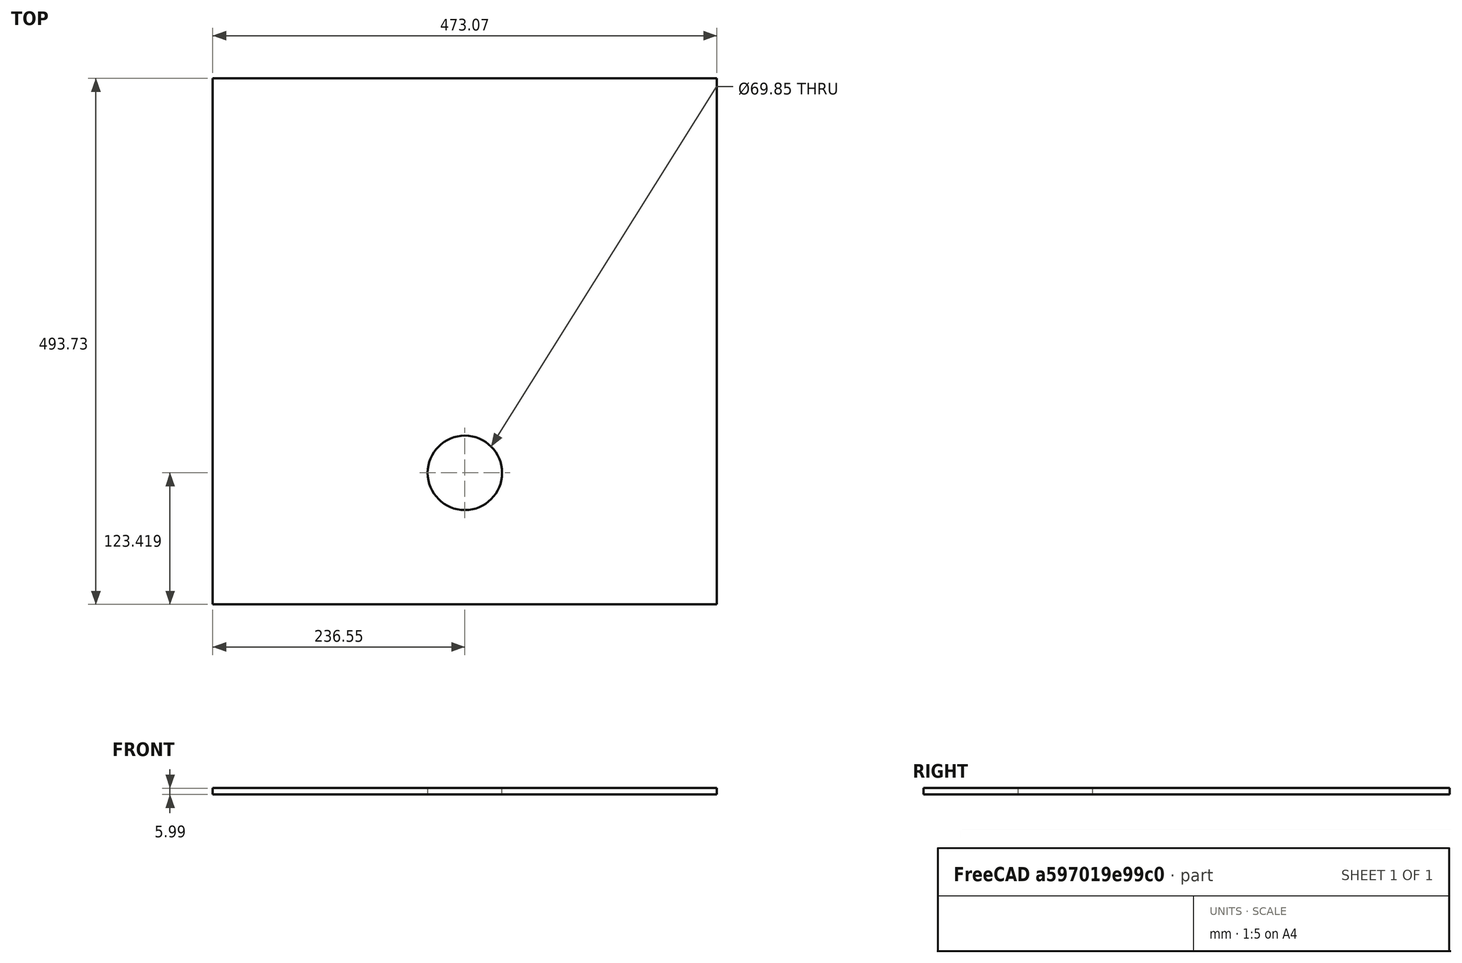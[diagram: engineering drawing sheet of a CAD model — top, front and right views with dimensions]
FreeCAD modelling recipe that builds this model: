
FCSTD DOCUMENT  (FreeCAD 0.19R24267 (Git))
Label: Up1-P3
License: All rights reserved
LicenseURL: http://en.wikipedia.org/wiki/All_rights_reserved
objects: TechDraw::DrawViewDimension×6, TechDraw::DrawProjGroupItem×2, TechDraw::DrawViewAnnotation×2, TechDraw::DrawHatch×2, Sketcher::SketchObject×1, Part::Extrusion×1, TechDraw::DrawSVGTemplate×1, TechDraw::DrawProjGroup×1, TechDraw::DrawPage×1
note: 2 computed .brp shape members not serialized (recipe doc carries the construction recipe); baked Part::Feature solids carry a one-line shape summary decoded from their .brp

FEATURE [Sketcher::SketchObject] Sketch
  FullyConstrained = true
  Placement = pos=(0,0,762) rot=(0,0,1;0rad)
  sketch-geometry (5):
    g0: LineSegment StartX=0 StartY=0 StartZ=0 EndX=473.075 EndY=0 EndZ=0
    g1: LineSegment StartX=473.075 StartY=0 StartZ=0 EndX=473.075 EndY=493.725 EndZ=0
    g2: LineSegment StartX=473.075 StartY=493.725 StartZ=0 EndX=0 EndY=493.725 EndZ=0
    g3: LineSegment StartX=0 StartY=493.725 StartZ=0 EndX=0 EndY=0 EndZ=0
    g4: Circle CenterX=236.55 CenterY=123.419 CenterZ=0 NormalX=0 NormalY=0 NormalZ=1 AngleXU=0 Radius=34.925
  constraints (14):
    c: Coincident(g0,g1)
    c: Coincident(g1,g2)
    c: Coincident(g2,g3)
    c: Coincident(g3,g0)
    c: Horizontal(g0)
    c: Horizontal(g2)
    c: Vertical(g1)
    c: Vertical(g3)
    c: Coincident(g0,g-1)
    c: DistanceX(g2,g2) = 473.075
    c: DistanceY(g3,g3) = 493.725
    c: DistanceY(g0,g4) = 123.419
    c: Distance(g4,g3) = 236.55
    c: Diameter(g4) = 69.85
FEATURE [Part::Extrusion] Extrude
  Base = -> Sketch
  Dir = (0,0,1)
  DirMode = 2
  FaceMakerClass = Part::FaceMakerBullseye
  LengthFwd = 5.9944
  LengthRev = 0
  Solid = true
  Symmetric = false
FEATURE [TechDraw::DrawSVGTemplate] Template
  Height = 215.9
  Orientation = 1
  Width = 279.4
FEATURE [TechDraw::DrawProjGroupItem] ProjItem  label="Front"
  CoarseView = false
  Direction = (0,0,1)
  Focus = 100
  HardHidden = false
  IsoCount = 0
  IsoHidden = false
  IsoVisible = false
  LockPosition = true
  Perspective = false
  Rotation = 0
  RotationVector = (1,0,0)
  Scale = 0.25
  ScaleType = 2
  SeamHidden = false
  SeamVisible = true
  SmoothHidden = false
  SmoothVisible = true
  Source = -> [Extrude]
  Type = 0
  X = 0
  XDirection = (1,0,0)
  Y = 0
FEATURE [TechDraw::DrawProjGroupItem] ProjItem001  label="Left"
  CoarseView = false
  Direction = (-1,0,1e-16)
  Focus = 100
  HardHidden = false
  IsoCount = 0
  IsoHidden = false
  IsoVisible = false
  LockPosition = false
  Perspective = false
  Rotation = 0
  RotationVector = (1,0,0)
  ScaleType = 2
  SeamHidden = false
  SeamVisible = true
  SmoothHidden = false
  SmoothVisible = true
  Source = -> [Extrude]
  Type = 1
  X = 88.5859
  XDirection = (1e-16,0,1)
  Y = 0
FEATURE [TechDraw::DrawProjGroup] ProjGroup
  Anchor = -> ProjItem
  AutoDistribute = true
  LockPosition = false
  ProjectionType = 0
  Rotation = 0
  Scale = 0.25
  ScaleType = 2
  Source = -> [Extrude]
  Views = -> [ProjItem,ProjItem001]
  X = 139.7
  Y = 107.95
  spacingX = 15.0114
  spacingY = 15.0114
FEATURE [TechDraw::DrawViewDimension] Dimension
  Arbitrary = false
  ArbitraryTolerances = false
  EqualTolerance = true
  FormatSpec = %.3f
  FormatSpecOverTolerance = %+.3f
  FormatSpecUnderTolerance = %+.3f
  Inverted = false
  LockPosition = false
  MeasureType = 1
  OverTolerance = 0
  References2D = -> [ProjItem]
  Rotation = 0
  ScaleType = 0
  TheoreticalExact = false
  Type = 1
  UnderTolerance = 0
  X = 0.805815
  Y = -69.7738
FEATURE [TechDraw::DrawViewDimension] Dimension001
  Arbitrary = false
  ArbitraryTolerances = false
  EqualTolerance = true
  FormatSpec = %.3f
  FormatSpecOverTolerance = %+.3f
  FormatSpecUnderTolerance = %+.3f
  Inverted = false
  LockPosition = false
  MeasureType = 1
  OverTolerance = 0
  References2D = -> [ProjItem001]
  Rotation = 0
  ScaleType = 0
  TheoreticalExact = false
  Type = 1
  UnderTolerance = 0
  X = 13.7182
  Y = 46.5357
FEATURE [TechDraw::DrawViewDimension] Dimension002
  Arbitrary = false
  ArbitraryTolerances = false
  EqualTolerance = true
  FormatSpec = %.3f
  FormatSpecOverTolerance = %+.3f
  FormatSpecUnderTolerance = %+.3f
  Inverted = false
  LockPosition = false
  MeasureType = 1
  OverTolerance = 0
  References2D = -> [ProjItem]
  Rotation = 0
  ScaleType = 0
  TheoreticalExact = false
  Type = 2
  UnderTolerance = 0
  X = 66.3867
  Y = 0.402907
FEATURE [TechDraw::DrawViewDimension] Dimension003
  Arbitrary = false
  ArbitraryTolerances = false
  EqualTolerance = true
  FormatSpec = %.3f
  FormatSpecOverTolerance = %+.3f
  FormatSpecUnderTolerance = %+.3f
  Inverted = false
  LockPosition = false
  MeasureType = 1
  OverTolerance = 0
  References2D = -> [ProjItem]
  Rotation = 0
  ScaleType = 0
  TheoreticalExact = false
  Type = 2
  UnderTolerance = 0
  X = 17.3858
  Y = -44.692
FEATURE [TechDraw::DrawViewDimension] Dimension004
  Arbitrary = false
  ArbitraryTolerances = false
  EqualTolerance = true
  FormatSpec = %.3f
  FormatSpecOverTolerance = %+.3f
  FormatSpecUnderTolerance = %+.3f
  Inverted = false
  LockPosition = false
  MeasureType = 1
  OverTolerance = 0
  References2D = -> [ProjItem]
  Rotation = 0
  ScaleType = 0
  TheoreticalExact = false
  Type = 1
  UnderTolerance = 0
  X = -26.3729
  Y = -5.14179
FEATURE [TechDraw::DrawViewDimension] Dimension005
  Arbitrary = false
  ArbitraryTolerances = false
  EqualTolerance = true
  FormatSpec = ⌀%.3f
  FormatSpecOverTolerance = %+.3f
  FormatSpecUnderTolerance = %+.3f
  Inverted = false
  LockPosition = false
  MeasureType = 1
  OverTolerance = 0
  References2D = -> [ProjItem]
  Rotation = 0
  ScaleType = 0
  TheoreticalExact = false
  Type = 5
  UnderTolerance = 0
  X = 18.2695
  Y = -6.7402
FEATURE [TechDraw::DrawViewAnnotation] Annotation
  Font = osifont
  LineSpace = 80
  LockPosition = false
  MaxWidth = -1
  Rotation = 0
  ScaleType = 0
  Text = Figure S3 (Upright) | Panel 3 [right side exterior baffle] | Quantity: 1
  TextSize = 5.0038
  TextStyle = 0
  X = 46.8492
  Y = 195.58
FEATURE [TechDraw::DrawViewAnnotation] Annotation001
  Font = osifont
  LineSpace = 80
  LockPosition = false
  MaxWidth = -1
  Rotation = 0
  ScaleType = 0
  Text = Units: Inches
  TextSize = 5.0038
  TextStyle = 0
  X = 259.08
  Y = 5.08
FEATURE [TechDraw::DrawPage] Page
  KeepUpdated = true
  NextBalloonIndex = 1
  ProjectionType = 0
  Template = -> Template
  Views = -> [ProjGroup,Dimension,Dimension001,Dimension002,Dimension003,Dimension004,Dimension005,Annotation,Annotation001]
FEATURE [TechDraw::DrawHatch] Hatch  label="HatchF0"
  HatchPattern = <path>
  Source = -> ProjItem001 [Face0]
FEATURE [TechDraw::DrawHatch] Hatch001  label="Hatch001F0"
  HatchPattern = <path>
  Source = -> ProjItem [Face0]
note: 2 file-system paths scrubbed to <path> (originals preserved in the JSON sidecar)
